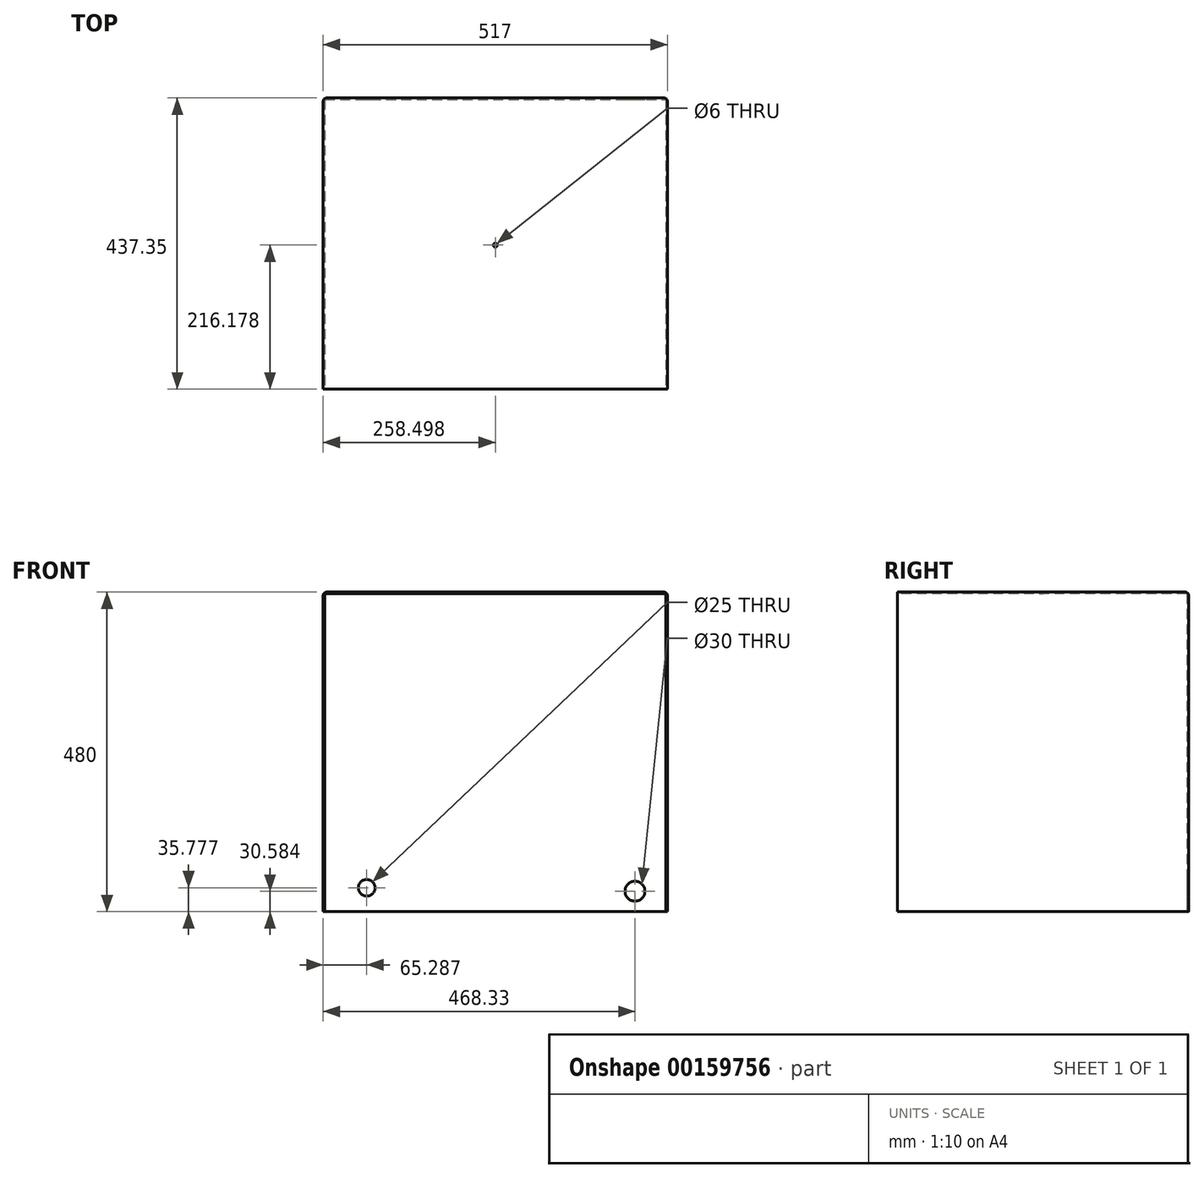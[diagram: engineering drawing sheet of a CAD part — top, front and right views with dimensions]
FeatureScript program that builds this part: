
annotation { "Feature Type Name" : "Feature", "Feature Type Description" : "" }
export const myFeature = defineFeature(function(context is Context, id is Id, definition is map)
    precondition{}
    {
        {
            var Q0;
            Q0=qCreatedBy(makeId("Top.planeOp"),FACE);
            var sketch = newSketch(context, id + "F0", { "sketchPlane" : qUnion([Q0])});
            skLineSegment(sketch, "E0.bottom", {"start": v(-104.18, 208.84) * mm, "end": v(412.82, 208.84) * mm});
            skLineSegment(sketch, "E0.top", {"start": v(-104.18, -228.5) * mm, "end": v(412.82, -228.5) * mm});
            skLineSegment(sketch, "E0.left", {"start": v(-104.18, 208.84) * mm, "end": v(-104.18, -228.5) * mm});
            skLineSegment(sketch, "E0.right", {"start": v(412.82, 208.84) * mm, "end": v(412.82, -228.5) * mm});
            skSolve(sketch);
        }
        {
            var Q0;
            Q0=makeQuery(id+"F0.imprint","IMPRINT",FACE,{"disambiguationData":[TD([[makeQuery(id+"F0.imprint","IMPRINT",EDGE,{"derivedFrom":sQuery(id+"F0.wireOp",EDGE,"E0.bottom")}),-1.0]])]});
            var Q1;
            Q1=sQuery(id+"F0.wireOp",EDGE,"E0.bottom");
            var Q2;
            Q2=sQuery(id+"F0.wireOp",EDGE,"E0.top");
            var Q3;
            Q3=sQuery(id+"F0.wireOp",EDGE,"E0.left");
            var Q4;
            Q4=sQuery(id+"F0.wireOp",EDGE,"E0.right");
            extrude(context, id + "F1", {"entities" : qUnion([Q0]), "surfaceEntities" : qUnion([Q1, Q2, Q3, Q4]), "depth" : 480 * mm});
        }
        {
            var Q0;
            Q0=makeQuery(id+"F1.opExtrude","SWEPT_FACE",FACE,{"disambiguationData":[OSD([sQuery(id+"F0.wireOp",EDGE,"E0.top")])]});
            var Q1;
            Q1=makeQuery(id+"F1.opExtrude","CAP_FACE",FACE,{"disambiguationData":[OSD([sQuery(id+"F0.wireOp",EDGE,"E0.bottom"),sQuery(id+"F0.wireOp",EDGE,"E0.top"),sQuery(id+"F0.wireOp",EDGE,"E0.left"),sQuery(id+"F0.wireOp",EDGE,"E0.right")])],"isStart":true});
            shell(context, id + "F2", {"entities" : qUnion([Q0, Q1]), "thickness" : 2.5 * mm});
        }
        {
            var Q0;
            Q0=makeQuery(id+"F1.opExtrude","CAP_EDGE",EDGE,{"disambiguationData":[OSD([sQuery(id+"F0.wireOp",EDGE,"E0.right")])],"isStart":false});
            var Q1;
            Q1=makeQuery(id+"F1.opExtrude","CAP_EDGE",EDGE,{"disambiguationData":[OSD([sQuery(id+"F0.wireOp",EDGE,"E0.left")])],"isStart":false});
            var Q2;
            Q2=makeQuery(id+"F1.opExtrude","SWEPT_EDGE",EDGE,{"disambiguationData":[OSD([sQuery(id+"F0.wireOp",EDGE,"E0.bottom"),sQuery(id+"F0.wireOp",EDGE,"E0.right")])]});
            var Q3;
            Q3=makeQuery(id+"F1.opExtrude","CAP_EDGE",EDGE,{"disambiguationData":[OSD([sQuery(id+"F0.wireOp",EDGE,"E0.bottom")])],"isStart":false});
            var Q4;
            Q4=makeQuery(id+"F1.opExtrude","SWEPT_EDGE",EDGE,{"disambiguationData":[OSD([sQuery(id+"F0.wireOp",EDGE,"E0.bottom"),sQuery(id+"F0.wireOp",EDGE,"E0.left")])]});
            fillet(context, id + "F3", {"entities" : qUnion([Q0, Q1, Q2, Q3, Q4]), "radius" : 5 * mm, "tangentPropagation" : true, "allowEdgeOverflow" : false});
        }
        {
            var Q0;
            Q0=makeQuery(id+"F1.opExtrude","SWEPT_FACE",FACE,{"disambiguationData":[OSD([sQuery(id+"F0.wireOp",EDGE,"E0.bottom")])]});
            var sketch = newSketch(context, id + "F4", { "sketchPlane" : qUnion([Q0])});
            skLineSegment(sketch, "E1.bottom", {"start": v(-407.82, 475) * mm, "end": v(99.18, 475) * mm});
            skLineSegment(sketch, "E1.top", {"start": v(-407.82, 0) * mm, "end": v(99.18, 0) * mm});
            skLineSegment(sketch, "E1.left", {"start": v(-407.82, 475) * mm, "end": v(-407.82, 0) * mm});
            skLineSegment(sketch, "E1.right", {"start": v(99.18, 475) * mm, "end": v(99.18, 0) * mm});
            skSolve(sketch);
        }
        {
            var Q0;
            Q0=makeQuery(id+"F4.imprint","IMPRINT",FACE,{"disambiguationData":[TD([[makeQuery(id+"F4.imprint","IMPRINT",EDGE,{"derivedFrom":sQuery(id+"F4.wireOp",EDGE,"E1.bottom")}),1.0]])]});
            var sketch = newSketch(context, id + "F5", { "sketchPlane" : qUnion([Q0])});
            skCircle(sketch, "E2", {"center": v(-364.15, 30.58) * mm, "radius": 15 * mm});
            skCircle(sketch, "E3", {"center": v(38.9, 35.78) * mm, "radius": 12.5 * mm});
            skSolve(sketch);
        }
        {
            var Q0;
            Q0=makeQuery(id+"F5.imprint","IMPRINT",FACE,{"disambiguationData":[TD([[makeQuery(id+"F5.imprint","IMPRINT",EDGE,{"derivedFrom":sQuery(id+"F5.wireOp",EDGE,"E2")}),1.0]])]});
            var Q1;
            Q1=makeQuery(id+"F5.imprint","IMPRINT",FACE,{"disambiguationData":[TD([[makeQuery(id+"F5.imprint","IMPRINT",EDGE,{"derivedFrom":sQuery(id+"F5.wireOp",EDGE,"E3")}),1.0]])]});
            extrude(context, id + "F6", {"entities" : qUnion([Q0, Q1]), "operationType" : NewBodyOperationType.REMOVE, "oppositeDirection" : true, "depth" : 11.75 * mm});
        }
        {
            var Q0;
            Q0=makeQuery(id+"F1.opExtrude","CAP_FACE",FACE,{"disambiguationData":[OSD([sQuery(id+"F0.wireOp",EDGE,"E0.bottom"),sQuery(id+"F0.wireOp",EDGE,"E0.top"),sQuery(id+"F0.wireOp",EDGE,"E0.left"),sQuery(id+"F0.wireOp",EDGE,"E0.right")])],"isStart":false});
            var sketch = newSketch(context, id + "F7", { "sketchPlane" : qUnion([Q0])});
            skCircle(sketch, "E4", {"center": v(154.32, -12.33) * mm, "radius": 3 * mm});
            skPoint(sketch, "E4.centerSnap0", {"position": v(-99.18, -12.33) * mm});
            skPoint(sketch, "E4.centerSnap1", {"position": v(154.32, 203.84) * mm});
            skSolve(sketch);
        }
        {
            var Q0;
            Q0=makeQuery(id+"F7.imprint","IMPRINT",FACE,{"disambiguationData":[TD([[makeQuery(id+"F7.imprint","IMPRINT",EDGE,{"derivedFrom":sQuery(id+"F7.wireOp",EDGE,"E4")}),1.0]])]});
            extrude(context, id + "F8", {"entities" : qUnion([Q0]), "operationType" : NewBodyOperationType.REMOVE, "oppositeDirection" : true, "depth" : 12.5 * mm});
        }
    });
